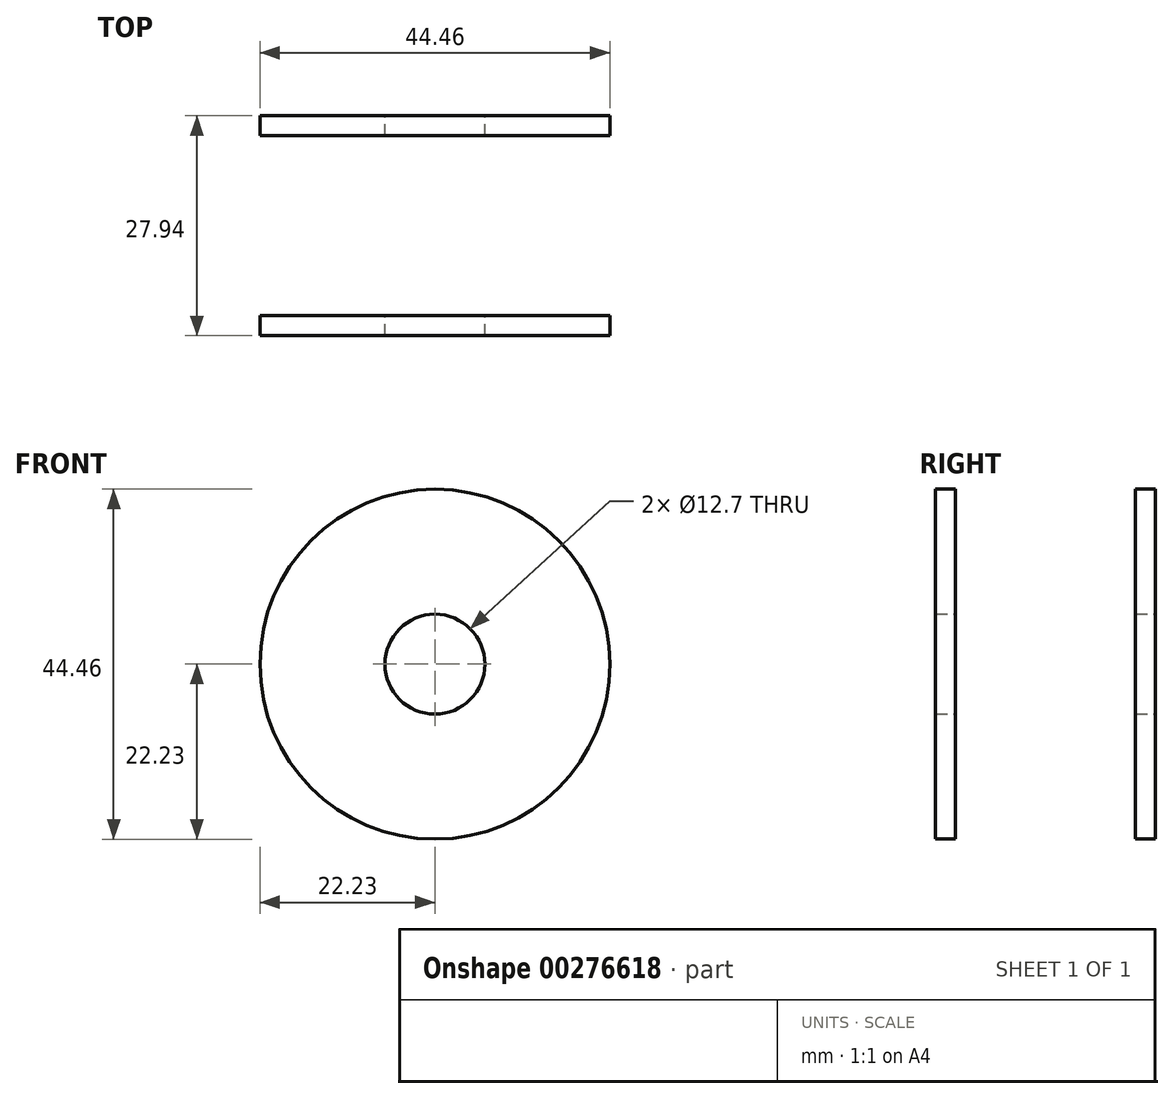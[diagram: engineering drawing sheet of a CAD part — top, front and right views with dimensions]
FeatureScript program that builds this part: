
annotation { "Feature Type Name" : "Feature", "Feature Type Description" : "" }
export const myFeature = defineFeature(function(context is Context, id is Id, definition is map)
    precondition{}
    {
        {
            var Q0;
            Q0=qCreatedBy(makeId("Front.planeOp"),FACE);
            var sketch = newSketch(context, id + "F0", { "sketchPlane" : qUnion([Q0])});
            skCircle(sketch, "E0", {"center": v(0, 0) * mm, "radius": 6.35 * mm});
            skCircle(sketch, "E1", {"center": v(0, 0) * mm, "radius": 22.23 * mm});
            skSolve(sketch);
        }
        {
            var Q0;
            Q0=makeQuery(id+"F0.imprint","IMPRINT",FACE,{"disambiguationData":[TD([[makeQuery(id+"F0.imprint","IMPRINT",EDGE,{"derivedFrom":sQuery(id+"F0.wireOp",EDGE,"E0")}),-1.0]])]});
            extrude(context, id + "F1", {"entities" : qUnion([Q0]), "depth" : 2.54 * mm});
        }
        {
            var Q0;
            Q0=qCreatedBy(makeId("Front.planeOp"),FACE);
            cPlane(context, id + "F2", {"entities" : qUnion([Q0]), "cplaneType" : CPlaneType.OFFSET, "offset" : 25.4 * mm, "width" : 152.4 * mm, "height" : 152.4 * mm});
        }
        {
            var Q0;
            Q0=qCreatedBy(id+"F2.planeOp",FACE);
            var sketch = newSketch(context, id + "F3", { "sketchPlane" : qUnion([Q0])});
            skCircle(sketch, "E2", {"center": v(0, 0) * mm, "radius": 6.35 * mm});
            skCircle(sketch, "E3", {"center": v(0, 0) * mm, "radius": 22.23 * mm});
            skSolve(sketch);
        }
        {
            var Q0;
            Q0=makeQuery(id+"F3.imprint","IMPRINT",FACE,{"disambiguationData":[TD([[makeQuery(id+"F3.imprint","IMPRINT",EDGE,{"derivedFrom":sQuery(id+"F3.wireOp",EDGE,"E2")}),-1.0]])]});
            extrude(context, id + "F4", {"entities" : qUnion([Q0]), "depth" : 2.54 * mm});
        }
    });
